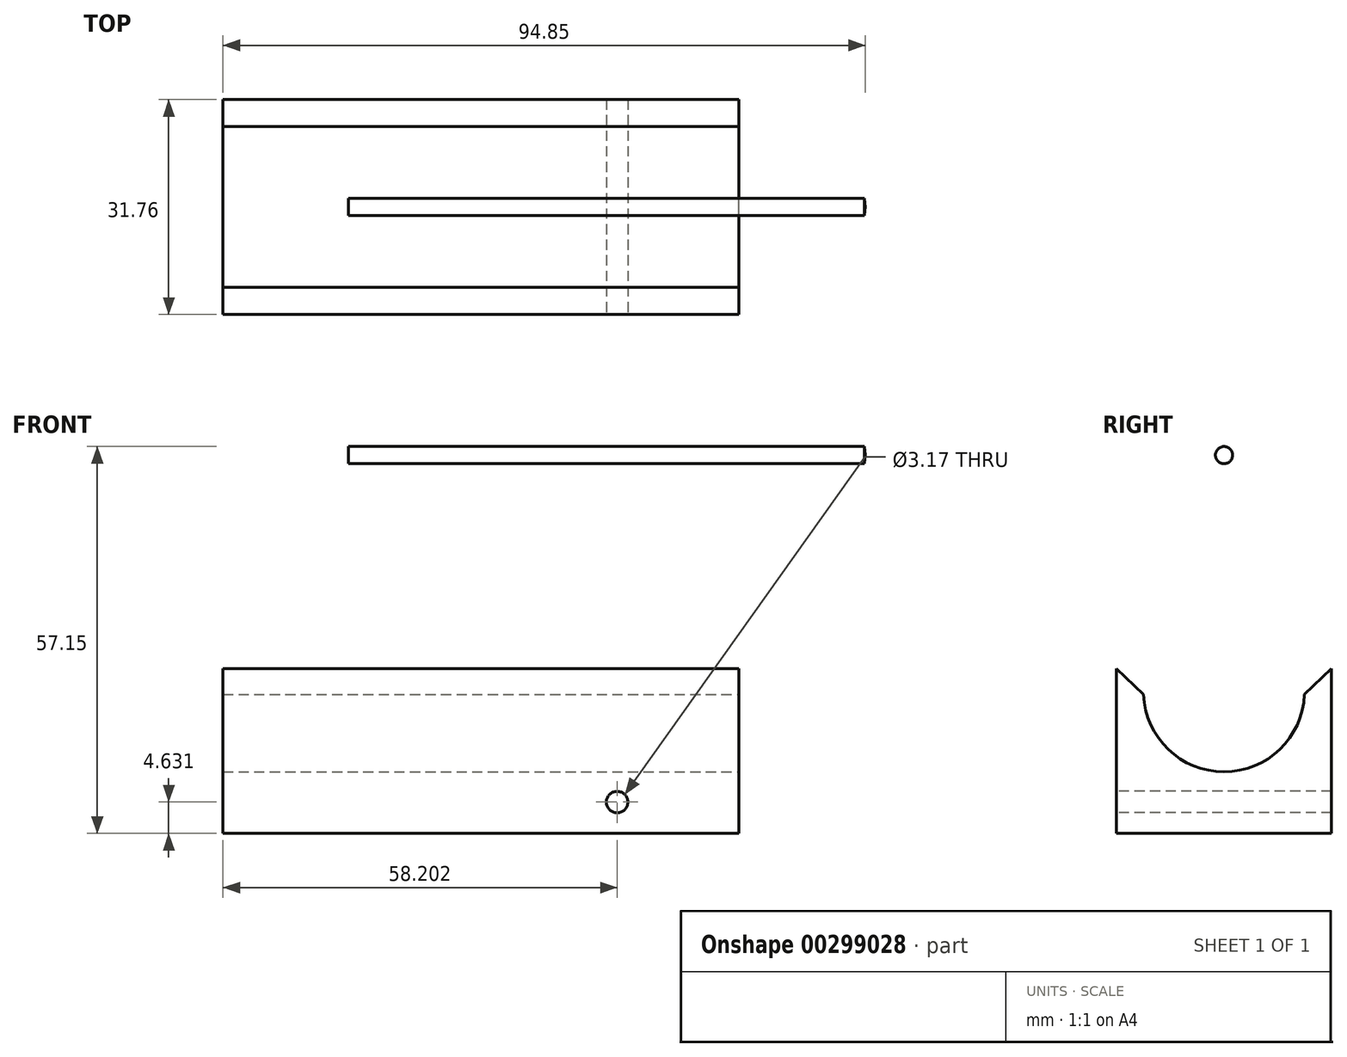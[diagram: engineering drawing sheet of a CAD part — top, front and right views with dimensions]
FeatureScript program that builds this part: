
annotation { "Feature Type Name" : "Feature", "Feature Type Description" : "" }
export const myFeature = defineFeature(function(context is Context, id is Id, definition is map)
    precondition{}
    {
        {
            var Q0;
            Q0=qCreatedBy(makeId("Front.planeOp"),FACE);
            var sketch = newSketch(context, id + "F0", { "sketchPlane" : qUnion([Q0])});
            skLineSegment(sketch, "E0", {"start": v(-44.2, 29.44) * mm, "end": v(32, 29.44) * mm});
            skLineSegment(sketch, "E1", {"start": v(32, 29.44) * mm, "end": v(32, 4.04) * mm});
            skLineSegment(sketch, "E2", {"start": v(32, 4.04) * mm, "end": v(-44.2, 4.04) * mm});
            skLineSegment(sketch, "E3", {"start": v(-44.2, 4.04) * mm, "end": v(-44.2, 29.44) * mm});
            skSolve(sketch);
        }
        {
            var Q0;
            Q0 = qSketchRegion(id + "F0", true);
            extrude(context, id + "F1", {"entities" : qUnion([Q0]), "endBound" : BoundingType.SYMMETRIC, "depth" : 31.75 * mm});
        }
        {
            var Q0;
            Q0=qCreatedBy(makeId("Right.planeOp"),FACE);
            var sketch = newSketch(context, id + "F2", { "sketchPlane" : qUnion([Q0])});
            skCircle(sketch, "E4", {"center": v(0, 25.03) * mm, "radius": 11.88 * mm});
            skSolve(sketch);
        }
        {
            var Q0;
            Q0 = qSketchRegion(id + "F2", true);
            extrude(context, id + "F3", {"entities" : qUnion([Q0]), "operationType" : NewBodyOperationType.REMOVE, "endBound" : BoundingType.SYMMETRIC, "oppositeDirection" : true, "depth" : 152.4 * mm});
        }
        {
            var Q0;
            Q0=makeQuery(id+"F3.boolean.opBoolean","INTERSECT",EDGE,{"disambiguationData":[OD(1.0)],"derivedFrom":[makeQuery(id+"F1.opExtrude","SWEPT_FACE",FACE,{"disambiguationData":[OSD([sQuery(id+"F0.wireOp",EDGE,"E0")])]}),makeQuery(id+"F3.opExtrude","SWEPT_FACE",FACE,{"disambiguationData":[OSD([sQuery(id+"F2.wireOp",EDGE,"E4")])]})]});
            var Q1;
            Q1=makeQuery(id+"F3.boolean.opBoolean","INTERSECT",EDGE,{"disambiguationData":[OD(0.0)],"derivedFrom":[makeQuery(id+"F1.opExtrude","SWEPT_FACE",FACE,{"disambiguationData":[OSD([sQuery(id+"F0.wireOp",EDGE,"E0")])]}),makeQuery(id+"F3.opExtrude","SWEPT_FACE",FACE,{"disambiguationData":[OSD([sQuery(id+"F2.wireOp",EDGE,"E4")])]})]});
            chamfer(context, id + "F4", {"entities" : qUnion([Q0, Q1]), "width" : 5.08 * mm, "tangentPropagation" : true});
        }
        {
            var Q0;
            Q0=qCreatedBy(makeId("Front.planeOp"),FACE);
            var sketch = newSketch(context, id + "F5", { "sketchPlane" : qUnion([Q0])});
            skCircle(sketch, "E5", {"center": v(14, 8.67) * mm, "radius": 1.59 * mm});
            skSolve(sketch);
        }
        {
            var Q0;
            Q0 = qSketchRegion(id + "F5", true);
            extrude(context, id + "F6", {"entities" : qUnion([Q0]), "operationType" : NewBodyOperationType.REMOVE, "endBound" : BoundingType.SYMMETRIC, "oppositeDirection" : true, "depth" : 152.4 * mm});
        }
        {
            var Q0;
            Q0=qCreatedBy(makeId("Front.planeOp"),FACE);
            var sketch = newSketch(context, id + "F7", { "sketchPlane" : qUnion([Q0])});
            skLineSegment(sketch, "E6", {"start": v(50.5, 61.2) * mm, "end": v(-25.7, 61.2) * mm});
            skLineSegment(sketch, "E7", {"start": v(-25.7, 61.2) * mm, "end": v(-25.7, 59.92) * mm});
            skLineSegment(sketch, "E8", {"start": v(-25.7, 59.92) * mm, "end": v(50.64, 59.92) * mm});
            skLineSegment(sketch, "E9", {"start": v(50.64, 59.92) * mm, "end": v(50.5, 61.2) * mm});
            skSolve(sketch);
        }
        {
            var Q0;
            Q0=makeQuery(id+"F7.imprint","IMPRINT",FACE,{"disambiguationData":[TD([[makeQuery(id+"F7.imprint","IMPRINT",EDGE,{"derivedFrom":sQuery(id+"F7.wireOp",EDGE,"E6")}),1.0]])]});
            var Q1;
            Q1=sQuery(id+"F7.wireOp",EDGE,"E8");
            revolve(context, id + "F8", {"entities" : qUnion([Q0]), "axis" : qUnion([Q1]), "revolveType" : RevolveType.FULL});
        }
    });
